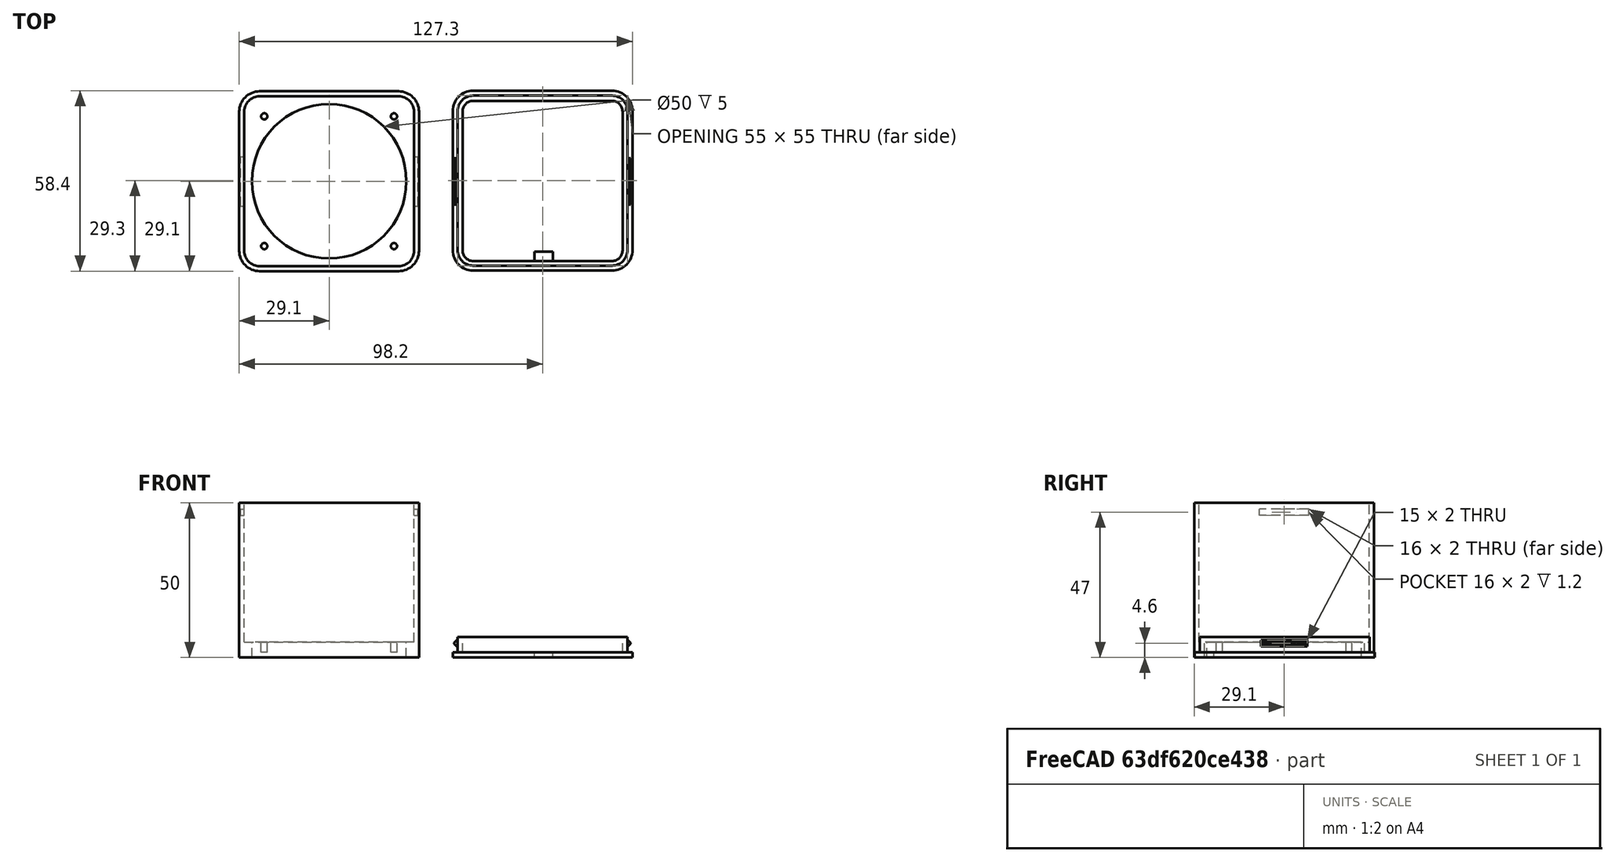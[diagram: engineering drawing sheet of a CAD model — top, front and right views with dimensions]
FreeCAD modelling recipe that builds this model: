
FCSTD DOCUMENT  (FreeCAD 0.16R)
Label: Speaker_52mm_2
License: All rights reserved
LicenseURL: http://en.wikipedia.org/wiki/All_rights_reserved
objects: Part::Box×9, Part::Cut×6, Part::Cylinder×5, Part::Fillet×5, Part::MultiFuse×5, Part::Chamfer×2
note: 32 computed .brp shape members not serialized (recipe doc carries the construction recipe); baked Part::Feature solids carry a one-line shape summary decoded from their .brp

FEATURE [Part::Cylinder] Cylinder  label="Zylinder"
  Angle = 360
  Height = 5
  Radius = 25
FEATURE [Part::Box] Box  label="Würfel"
  Height = 50
  Length = 55
  Placement = pos=(-27.5,-27.5,5) rot=(0,0,1;0rad)
  Width = 55
FEATURE [Part::Box] Box001  label="Würfel001"
  Height = 50
  Length = 58.2
  Placement = pos=(-29.1,-29.1,0) rot=(0,0,1;0rad)
  Width = 58.2
FEATURE [Part::Cut] Cut
  Base = -> Box001
  Tool = -> Box
FEATURE [Part::Cut] Cut001
  Base = -> Cut
  Tool = -> Cylinder
FEATURE [Part::Fillet] Fillet
  Base = -> Cut001
  Edges = 4 edges r=5: [Edge18,Edge19,Edge21,Edge23]
FEATURE [Part::Fillet] Fillet001
  Base = -> Fillet
  Edges = 4 edges r=6.6: [Edge29,Edge30,Edge33,Edge35]
FEATURE [Part::Cylinder] Cylinder001  label="Zylinder001"
  Angle = 360
  Height = 10
  Placement = pos=(21,21,1.6) rot=(0,0,1;0rad)
  Radius = 1
FEATURE [Part::Cylinder] Cylinder002  label="Zylinder002"
  Angle = 360
  Height = 10
  Placement = pos=(21,-21,1.6) rot=(0,0,1;0rad)
  Radius = 1
FEATURE [Part::Cylinder] Cylinder003  label="Zylinder003"
  Angle = 360
  Height = 10
  Placement = pos=(-21,21,1.6) rot=(0,0,1;0rad)
  Radius = 1
FEATURE [Part::Cylinder] Cylinder004  label="Zylinder004"
  Angle = 360
  Height = 10
  Placement = pos=(-21,-21,1.6) rot=(0,0,1;0rad)
  Radius = 1
FEATURE [Part::MultiFuse] Fusion
  Shapes = -> [Cylinder004,Cylinder003,Cylinder002,Cylinder001]
FEATURE [Part::Cut] Cut002
  Base = -> Fillet001
  Tool = -> Fusion
FEATURE [Part::Box] Box002  label="Würfel002"
  Height = 1.6
  Length = 58.2
  Placement = pos=(40,-28.9,0) rot=(0,0,1;0rad)
  Width = 58.2
FEATURE [Part::Box] Box003  label="Würfel003"
  Height = 6.6
  Length = 55
  Placement = pos=(41.6,-27.3,0) rot=(0,0,1;0rad)
  Width = 55
FEATURE [Part::Box] Box004  label="Würfel004"
  Height = 5
  Length = 51.8
  Placement = pos=(43.2,-25.8,1.6) rot=(0,0,1;0rad)
  Width = 51.8
FEATURE [Part::Cut] Cut003
  Base = -> Box003
  Tool = -> Box004
FEATURE [Part::Fillet] Fillet002
  Base = -> Box002
  Edges = 4 edges r=6.6: [Edge1,Edge3,Edge5,Edge7]
FEATURE [Part::Fillet] Fillet003
  Base = -> Cut003
  Edges = 4 edges r=3.4: [Edge17,Edge19,Edge21,Edge22]
FEATURE [Part::Fillet] Fillet004
  Base = -> Fillet003
  Edges = 4 edges r=5: [Edge29,Edge30,Edge33,Edge35]
FEATURE [Part::MultiFuse] Fusion001
  Shapes = -> [Fillet002,Fillet004]
FEATURE [Part::Box] Box005  label="Würfel005"
  Height = 10
  Length = 6
  Placement = pos=(66.5,-25.8,0) rot=(0,0,1;0rad)
  Width = 3
FEATURE [Part::Cut] Cut004
  Base = -> Fusion001
  Tool = -> Box005
FEATURE [Part::MultiFuse] Fusion002
  Shapes = -> [Cut002,Cut004]
FEATURE [Part::Box] Box006  label="Würfel006"
  Height = 2
  Length = 57.4
  Placement = pos=(-28.7,-8,46) rot=(0,0,1;0rad)
  Width = 16
FEATURE [Part::Box] Box007  label="Würfel007"
  Height = 2
  Length = 1.2
  Placement = pos=(40.4,-7.5,3.6) rot=(0,0,1;0rad)
  Width = 15
FEATURE [Part::Box] Box008  label="Würfel008"
  Height = 2
  Length = 1.2
  Placement = pos=(96.4,-7.5,3.6) rot=(0,0,1;0rad)
  Width = 15
FEATURE [Part::Chamfer] Chamfer
  Base = -> Box007
  Edges = 2 edges r=0.9: [Edge2,Edge4]
FEATURE [Part::Chamfer] Chamfer001
  Base = -> Box008
  Edges = 2 edges r=0.9: [Edge6,Edge8]
FEATURE [Part::MultiFuse] Fusion003
  Shapes = -> [Chamfer,Chamfer001]
FEATURE [Part::Cut] Cut005
  Base = -> Fusion002
  Tool = -> Box006
FEATURE [Part::MultiFuse] Fusion004
  Shapes = -> [Fusion003,Cut005]
